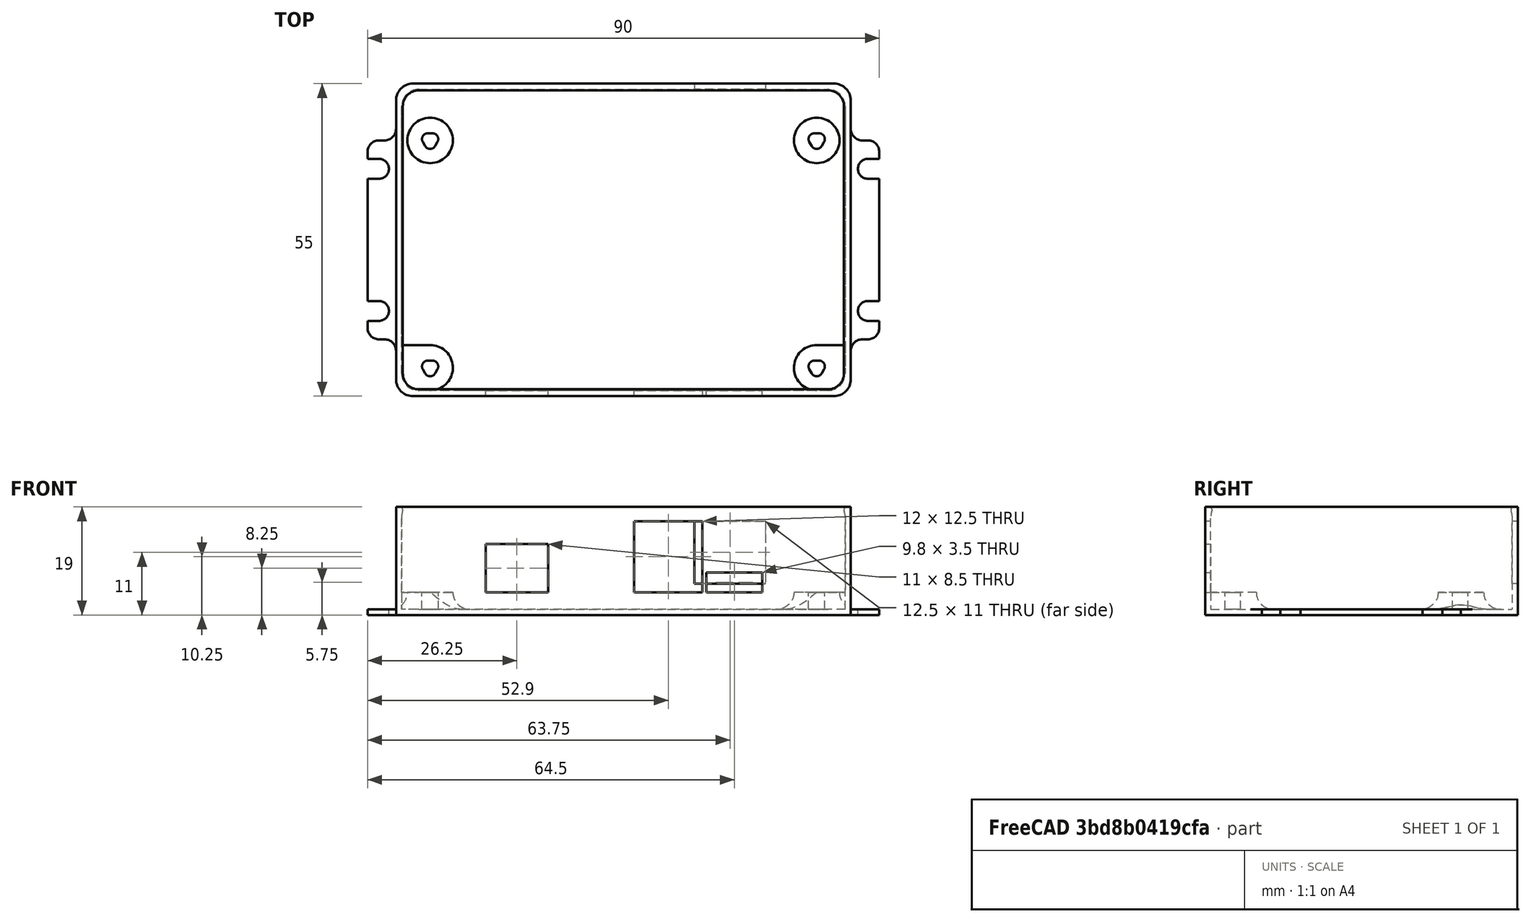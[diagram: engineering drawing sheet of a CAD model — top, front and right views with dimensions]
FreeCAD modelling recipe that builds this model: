
FCSTD DOCUMENT  (FreeCAD 0.21R32457 (Git))
Label: board outline
License: All rights reserved
LicenseURL: http://en.wikipedia.org/wiki/All_rights_reserved
objects: Part::Feature×1, Sketcher::SketchObject×1
note: 2 computed .brp shape members not serialized (recipe doc carries the construction recipe); baked Part::Feature solids carry a one-line shape summary decoded from their .brp

FEATURE [Part::Feature] Solid  label="box"
  Placement = pos=(0,0,0) rot=(0.57735,0.57735,0.57735;2.0944rad)
  shape: bbox 90.01 x 59.89 x 19.01 mm, 137 faces (baked)
FEATURE [Sketcher::SketchObject] Sketch
  ExternalGeometry = -> [Solid]
  FullyConstrained = false
  sketch-geometry (14):
    g0: Circle CenterX=-71 CenterY=-8.5 CenterZ=0 NormalX=0 NormalY=0 NormalZ=1 AngleXU=0 Radius=1.6
    g1: Circle CenterX=-3 CenterY=-8.5 CenterZ=0 NormalX=0 NormalY=0 NormalZ=1 AngleXU=0 Radius=1.6
    g2: ArcOfCircle CenterX=-73 CenterY=-2.5 CenterZ=0 NormalX=0 NormalY=0 NormalZ=1 AngleXU=0 Radius=2 StartAngle=1.5708 EndAngle=3.14159
    g3: LineSegment StartX=-73 StartY=-0.5 StartZ=0 EndX=-1 EndY=-0.5 EndZ=0
    g4: ArcOfCircle CenterX=-1 CenterY=-2.5 CenterZ=0 NormalX=0 NormalY=0 NormalZ=1 AngleXU=0 Radius=2 StartAngle=2e-16 EndAngle=1.5708
    g5: LineSegment StartX=1 StartY=-2.5 StartZ=0 EndX=1 EndY=-49.5 EndZ=0
    g6: ArcOfCircle CenterX=-1 CenterY=-49.5 CenterZ=0 NormalX=0 NormalY=0 NormalZ=1 AngleXU=0 Radius=2 StartAngle=4.71239 EndAngle=6.28319
    g7: LineSegment StartX=-1 StartY=-51.5 StartZ=0 EndX=-73 EndY=-51.5 EndZ=0
    g8: ArcOfCircle CenterX=-73 CenterY=-49.5 CenterZ=0 NormalX=0 NormalY=0 NormalZ=1 AngleXU=0 Radius=2 StartAngle=3.14159 EndAngle=4.71239
    g9: LineSegment StartX=-75 StartY=-49.5 StartZ=0 EndX=-75 EndY=-2.5 EndZ=0
    g10: GeomPoint X=-75 Y=-0.5 Z=0
    g11: GeomPoint X=1 Y=-51.5 Z=0
    g12: Circle CenterX=-71 CenterY=-48.5 CenterZ=0 NormalX=0 NormalY=0 NormalZ=1 AngleXU=0 Radius=1.6
    g13: Circle CenterX=-3 CenterY=-48.5 CenterZ=0 NormalX=0 NormalY=0 NormalZ=1 AngleXU=0 Radius=1.6
  constraints (28):
    c: Tangent(g2,g3) = 1.5708
    c: Tangent(g3,g4) = 1.5708
    c: Tangent(g4,g5) = 1.5708
    c: Tangent(g5,g6) = 1.5708
    c: Tangent(g6,g7) = 1.5708
    c: Tangent(g7,g8) = 1.5708
    c: Tangent(g8,g9) = 1.5708
    c: Tangent(g9,g2) = 1.5708
    c: Horizontal(g3)
    c: Horizontal(g7)
    c: Vertical(g5)
    c: Vertical(g9)
    c: Equal(g2,g4)
    c: Equal(g4,g6)
    c: Equal(g6,g8)
    c: PointOnObject(g10,g3)
    c: PointOnObject(g10,g9)
    c: PointOnObject(g11,g5)
    c: PointOnObject(g11,g7)
    c: Coincident(g6,g-8)
    c: Coincident(g2,g-7)
    c: DistanceX(g-7,g2) = 1
    c: Coincident(g12,g-6)
    c: Coincident(g13,g-5)
    c: Equal(g12,g0)
    c: Equal(g0,g1)
    c: Equal(g1,g13)
    c: Diameter(g0) = 3.2
